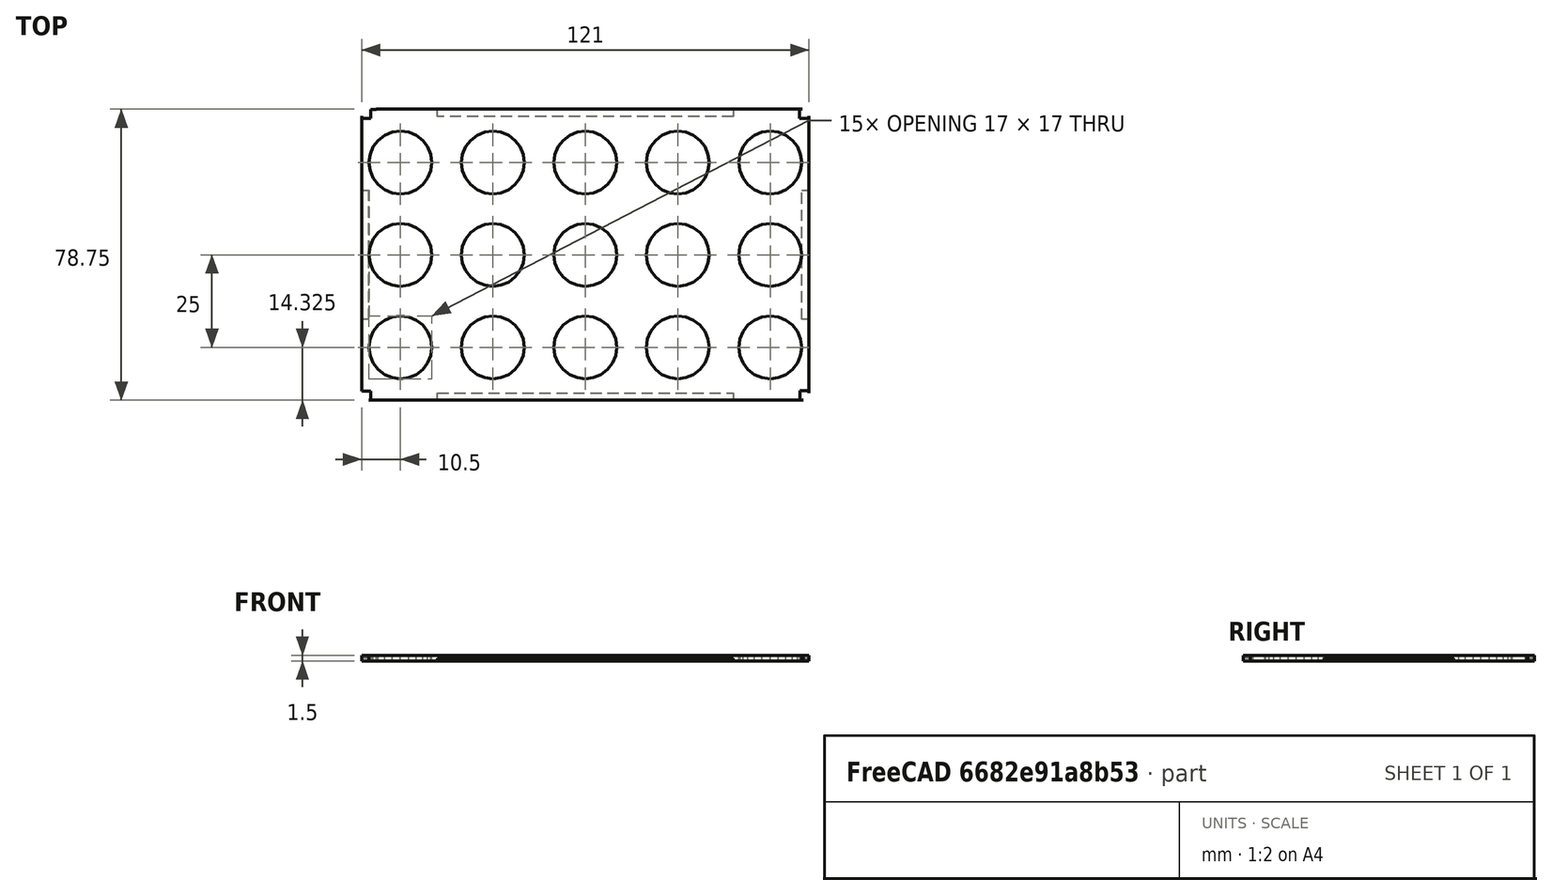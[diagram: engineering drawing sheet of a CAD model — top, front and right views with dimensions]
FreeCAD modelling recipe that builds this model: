
FCSTD DOCUMENT  (FreeCAD 0.21R33694 (Git))
Label: bottm_part_15_tubes
License: All rights reserved
LicenseURL: http://en.wikipedia.org/wiki/All_rights_reserved
objects: Part::Feature×2, Part::Box×2, Part::Common×2, Sketcher::SketchObject×2, PartDesign::Body×2, Mesh::Feature×1, Part::Mirroring×1, Part::Fuse×1, Part::Refine×1, PartDesign::FeatureBase×1, PartDesign::Pocket×1
note: 16 computed .brp shape members not serialized (recipe doc carries the construction recipe); baked Part::Feature solids carry a one-line shape summary decoded from their .brp

FEATURE [Mesh::Feature] Opentrons_15mL_Tube_Rack_Top
FEATURE [Part::Feature] Opentrons_15mL_Tube_Rack_Top001
  Placement = pos=(0,0,-0.3) rot=(0,0,1;0rad)
  shape: bbox 121 x 78.75 x 10 mm, 1658 faces, 0 solids (baked)
FEATURE [Part::Box] Box  label="Cube"
  AttacherType = Attacher::AttachEngine3D
  Height = 1.5
  Length = 130
  Placement = pos=(-3.8,-5.5,0) rot=(0,0,1;0rad)
  Width = 90
FEATURE [Part::Feature] Opentrons_15mL_Tube_Rack_Top001_solid  label="Rack_Top_Solid"
  shape: bbox 121 x 78.75 x 10 mm, 1658 faces (baked)
FEATURE [Part::Common] Common
  Base = -> Box
  Placement = pos=(0,0,-24.1) rot=(0,0,1;0rad)
  Tool = -> Opentrons_15mL_Tube_Rack_Top001_solid
FEATURE [Part::Box] Box001  label="Cube001"
  AttacherType = Attacher::AttachEngine3D
  Height = 10
  Length = 10
  Placement = pos=(0,0,-29) rot=(0,0,1;0rad)
  Width = 10
FEATURE [Part::Common] Common001  label="coin"
  Base = -> Common
  Tool = -> Box001
FEATURE [Part::Mirroring] Part__Mirroring  label="coin (Mirror #1)"
  Base = (0,0,0)
  Normal = (0,1,0)
  Placement = pos=(0,78.7,0) rot=(0,0,1;0rad)
  Source = -> Common001
FEATURE [Part::Fuse] Fusion
  Base = -> Common
  Tool = -> Part__Mirroring
FEATURE [Part::Refine] Fusion001
  Source = -> Fusion
FEATURE [Sketcher::SketchObject] Sketch
  FullyConstrained = true
  MapMode = 5
  Support = -> [XY_Plane]
FEATURE [PartDesign::Body] Body
  Group = -> [Sketch]
  Origin = -> Origin
FEATURE [PartDesign::FeatureBase] BaseFeature
  BaseFeature = -> Fusion001
FEATURE [Sketcher::SketchObject] Sketch001
  ExternalGeometry = -> [BaseFeature]
  FullyConstrained = false
  MapMode = 5
  Placement = pos=(0,0,-22.6) rot=(0,0,1;0rad)
  Support = -> [BaseFeature]
  sketch-geometry (20):
    g0: LineSegment StartX=0.024901 StartY=78.7963 StartZ=0 EndX=2.5249 EndY=78.7963 EndZ=0
    g1: LineSegment StartX=2.5249 StartY=78.7963 StartZ=0 EndX=2.5249 EndY=76.2963 EndZ=0
    g2: LineSegment StartX=2.5249 StartY=76.2963 StartZ=0 EndX=0.024901 EndY=76.2963 EndZ=0
    g3: LineSegment StartX=0.024901 StartY=76.2963 StartZ=0 EndX=0.024901 EndY=78.7963 EndZ=0
    g4: LineSegment StartX=118.476 StartY=78.727 StartZ=0 EndX=120.976 EndY=78.727 EndZ=0
    g5: LineSegment StartX=120.976 StartY=78.727 StartZ=0 EndX=120.976 EndY=76.227 EndZ=0
    g6: LineSegment StartX=120.976 StartY=76.227 StartZ=0 EndX=118.476 EndY=76.227 EndZ=0
    g7: LineSegment StartX=118.476 StartY=76.227 StartZ=0 EndX=118.476 EndY=78.727 EndZ=0
    g8: LineSegment StartX=118.495 StartY=2.55349 StartZ=0 EndX=120.995 EndY=2.55349 EndZ=0
    g9: LineSegment StartX=120.995 StartY=2.55349 StartZ=0 EndX=120.995 EndY=0.053491 EndZ=0
    g10: LineSegment StartX=120.995 StartY=0.053491 StartZ=0 EndX=118.495 EndY=0.053491 EndZ=0
    g11: LineSegment StartX=118.495 StartY=0.053491 StartZ=0 EndX=118.495 EndY=2.55349 EndZ=0
    g12: LineSegment StartX=-93.1564 StartY=26.8703 StartZ=0 EndX=-90.6564 EndY=26.8703 EndZ=0
    g13: LineSegment StartX=-90.6564 StartY=26.8703 StartZ=0 EndX=-90.6564 EndY=24.3703 EndZ=0
    g14: LineSegment StartX=-90.6564 StartY=24.3703 StartZ=0 EndX=-93.1564 EndY=24.3703 EndZ=0
    g15: LineSegment StartX=-93.1564 StartY=24.3703 StartZ=0 EndX=-93.1564 EndY=26.8703 EndZ=0
    g16: LineSegment StartX=2.48483 StartY=2.50592 StartZ=0 EndX=2.48483 EndY=0.005919 EndZ=0
    g17: LineSegment StartX=-0.015171 StartY=2.50592 StartZ=0 EndX=2.48483 EndY=2.50592 EndZ=0
    g18: LineSegment StartX=-0.015171 StartY=0.005919 StartZ=0 EndX=-0.015171 EndY=2.50592 EndZ=0
    g19: LineSegment StartX=2.48483 StartY=0.005919 StartZ=0 EndX=-0.015171 EndY=0.005919 EndZ=0
  constraints (50):
    c: Coincident(g0,g1)
    c: Coincident(g1,g2)
    c: Coincident(g2,g3)
    c: Coincident(g3,g0)
    c: Horizontal(g0)
    c: Horizontal(g2)
    c: Vertical(g1)
    c: Vertical(g3)
    c: DistanceX(g0,g0) = 2.5
    c: DistanceY(g2,g0) = 2.5
    c: Coincident(g4,g5)
    c: Coincident(g5,g6)
    c: Coincident(g6,g7)
    c: Coincident(g7,g4)
    c: Horizontal(g4)
    c: Horizontal(g6)
    c: Vertical(g5)
    c: Vertical(g7)
    c: Equal(g0,g4) = 2.5
    c: DistanceY(g6,g4) = 2.5
    c: Coincident(g8,g9)
    c: Coincident(g9,g10)
    c: Coincident(g10,g11)
    c: Coincident(g11,g8)
    c: Horizontal(g8)
    c: Horizontal(g10)
    c: Vertical(g9)
    c: Vertical(g11)
    c: Equal(g0,g8) = 2.5
    c: DistanceY(g10,g8) = 2.5
    c: Coincident(g12,g13)
    c: Coincident(g13,g14)
    c: Coincident(g14,g15)
    c: Coincident(g15,g12)
    c: Horizontal(g12)
    c: Horizontal(g14)
    c: Vertical(g13)
    c: Vertical(g15)
    c: Equal(g0,g12) = 2.5
    c: DistanceY(g14,g12) = 2.5
    c: Coincident(g17,g16)
    c: Coincident(g16,g19)
    c: Coincident(g19,g18)
    c: Coincident(g18,g17)
    c: Horizontal(g17)
    c: Horizontal(g19)
    c: Vertical(g16)
    c: Vertical(g18)
    c: Equal(g0,g17) = 2.5
    c: DistanceY(g19,g17) = 2.5
FEATURE [PartDesign::Pocket] Pocket
  BaseFeature = -> BaseFeature
  Direction = (0,0,-1)
  Length = 5
  Length2 = 5
  Profile = -> Sketch001
  ReferenceAxis = -> Sketch001 [N_Axis]
  Type = 0
FEATURE [PartDesign::Body] Body001
  BaseFeature = -> Fusion001
  Group = -> [BaseFeature,Sketch001,Pocket]
  Origin = -> Origin001
  Tip = -> Pocket
